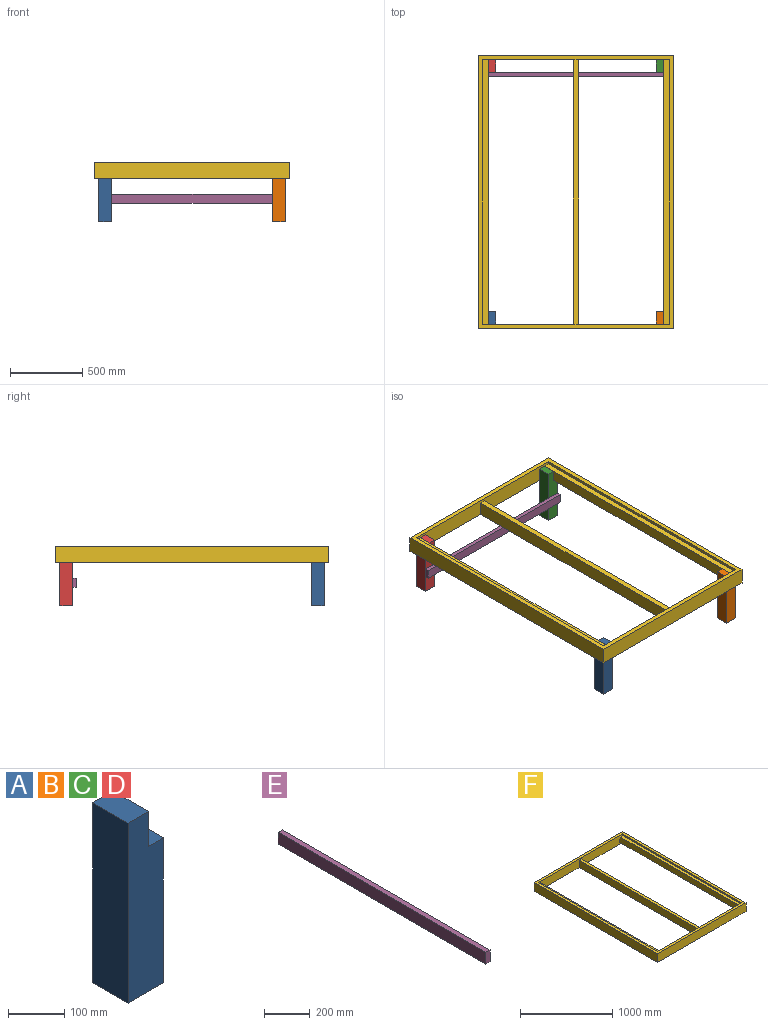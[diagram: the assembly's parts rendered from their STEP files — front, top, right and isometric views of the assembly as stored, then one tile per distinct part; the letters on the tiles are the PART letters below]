
ASSEMBLY  parts=6 mates=5
PART A: 8 faces, bbox 88.9x88.9x390.5 mm
  f0: plane 314.33x88.9mm, normal (1,0,0), area 27943.5mm2, adj f1,f3,f5,f7
  f1: plane 390.53x88.9mm, normal (0,1,0), area 31814.5mm2, adj f0,f2,f4,f5,f6,f7
  f2: plane 390.53x88.9mm, normal (-1,0,0), area 34717.7mm2, adj f1,f3,f4,f5
  f3: plane 390.53x88.9mm, normal (0,-1,0), area 31814.5mm2, adj f0,f2,f4,f5,f6,f7
  f4: plane 88.9x50.8mm, normal (0,0,1), area 4516.1mm2, adj f1,f2,f3,f6
  f5: plane 88.9x88.9mm, normal (0,0,-1), area 7903.2mm2, adj f0,f1,f2,f3
  f6: plane 88.9x76.2mm, normal (1,0,0), area 6774.2mm2, adj f1,f3,f4,f7
  f7: plane 88.9x38.1mm, normal (0,0,1), area 3387.1mm2, adj f0,f1,f3,f6
PART B: same geometry as A
PART C: same geometry as A
PART D: same geometry as A
PART E: 6 faces, bbox 25.4x1289.1x63.5 mm
  f0: plane 1289.05x63.5mm, normal (-1,0,0), area 81854.7mm2, adj f1,f3,f4,f5
  f1: plane 63.5x25.4mm, normal (0,-1,0), area 1612.9mm2, adj f0,f2,f4,f5
  f2: plane 1289.05x63.5mm, normal (1,0,0), area 81854.7mm2, adj f1,f3,f4,f5
  f3: plane 63.5x25.4mm, normal (0,1,0), area 1612.9mm2, adj f0,f2,f4,f5
  f4: plane 1289.05x25.4mm, normal (0,0,1), area 32741.9mm2, adj f0,f1,f2,f3
  f5: plane 1289.05x25.4mm, normal (0,0,-1), area 32741.9mm2, adj f0,f1,f2,f3
PART F: 21 faces, bbox 1352.6x1889.1x114.3 mm
  f0: plane 1289.05x114.3mm, normal (0,-1,0), area 137903mm2, adj f1,f3,f7,f8,f10,f11,f12,f13
  f1: plane 1825.63x19.05mm, normal (-1,0,0), area 34778.2mm2, adj f0,f2,f10,f15
  f2: plane 1289.05x114.3mm, normal (0,1,0), area 137902.9mm2, adj f1,f3,f7,f8,f10,f11,f12,f13
  f3: plane 1825.63x19.05mm, normal (1,0,0), area 34778.2mm2, adj f0,f2,f11,f12
  f4: plane 1352.55x114.3mm, normal (0,-1,0), area 154596.5mm2, adj f5,f9,f10,f11
  f5: plane 1889.13x114.3mm, normal (1,0,0), area 215927mm2, adj f4,f6,f10,f11
  f6: plane 1352.55x114.3mm, normal (0,1,0), area 154596.5mm2, adj f5,f9,f10,f11
  f7: plane 1825.63x19.05mm, normal (-1,0,0), area 34778.2mm2, adj f0,f2,f11,f16
  f8: plane 1825.63x19.05mm, normal (1,0,0), area 34778.2mm2, adj f0,f2,f10,f13
  f9: plane 1889.13x114.3mm, normal (-1,0,0), area 215927mm2, adj f4,f6,f10,f11
  f10: plane 1889.13x1352.55mm, normal (0,0,1), area 201814.1mm2, adj f0,f1,f2,f4,f5,f6,f8,f9
  f11: plane 1889.13x1352.55mm, normal (0,0,-1), area 271370.4mm2, adj f0,f2,f3,f4,f5,f6,f7,f9
  f12: plane 1825.63x38.1mm, normal (0,0,-1), area 69556.3mm2, adj f0,f2,f3,f14
  f13: plane 1825.63x38.1mm, normal (0,0,1), area 69556.3mm2, adj f0,f2,f8,f14
  f14: plane 1825.63x76.2mm, normal (1,0,0), area 139112.6mm2, adj f0,f2,f12,f13
  f15: plane 1825.63x38.1mm, normal (0,0,1), area 69556.3mm2, adj f0,f1,f2,f17
  f16: plane 1825.63x38.1mm, normal (0,0,-1), area 69556.3mm2, adj f0,f2,f7,f17
  f17: plane 1825.63x76.2mm, normal (-1,0,0), area 139112.6mm2, adj f0,f2,f15,f16
  f18: plane 1825.63x38.1mm, normal (0,0,1), area 69556.3mm2, adj f0,f2,f19,f20
  f19: plane 1825.63x95.25mm, normal (-1,0,0), area 173890.8mm2, adj f0,f2,f11,f18
  f20: plane 1825.63x95.25mm, normal (1,0,0), area 173890.8mm2, adj f0,f2,f11,f18
PLACE A rot(axis=(0,0,1),180deg) t=(-594.22,-859.6,-344.36)mm
PLACE B t=(605.93,-859.6,-344.36)mm
PLACE C t=(605.93,877.12,-344.36)mm
PLACE D rot(axis=(0,0,-1),180deg) t=(-594.22,877.12,-344.36)mm
PLACE E rot(axis=(-0.71,-0.71,0),180deg) t=(-638.67,807.27,-155.45)mm
PLACE F t=(5.86,8.76,-49.08)mm
MATE fastened B.f7 <-> F.f16  axis (0,0,1) through (612.28,-904.05,-30.03)mm
MATE fastened E.f2 <-> D.f1  axis (0,1,0) through (-638.67,832.67,-187.2)mm
MATE fastened D.f7 <-> F.f12  axis (0,0,1) through (-600.57,921.57,-30.03)mm
MATE fastened C.f7 <-> F.f16  axis (0,0,1) through (612.28,921.57,-30.03)mm
MATE fastened A.f7 <-> F.f12  axis (0,0,1) through (-600.57,-904.05,-30.03)mm
